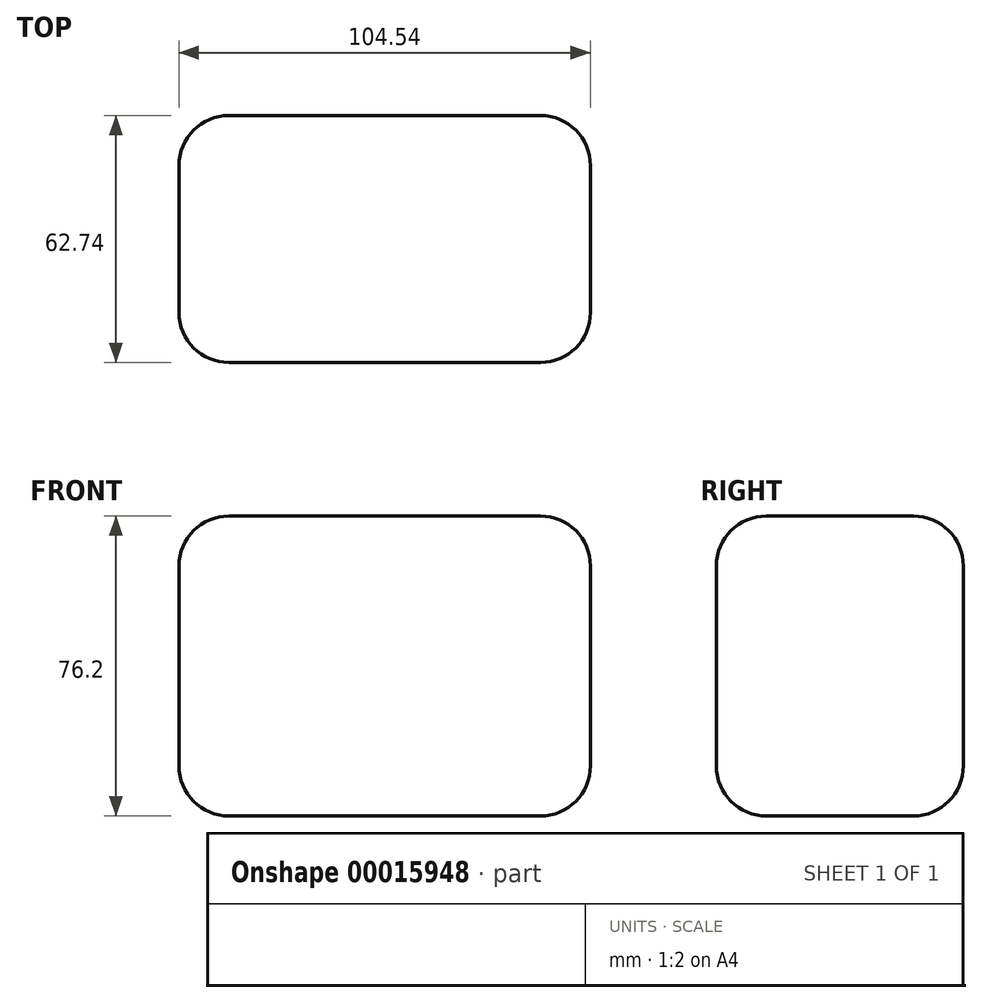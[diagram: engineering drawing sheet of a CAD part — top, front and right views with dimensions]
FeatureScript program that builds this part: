
annotation { "Feature Type Name" : "Feature", "Feature Type Description" : "" }
export const myFeature = defineFeature(function(context is Context, id is Id, definition is map)
    precondition{}
    {
        {
            var Q0;
            Q0=qCreatedBy(makeId("Top.planeOp"),FACE);
            var sketch = newSketch(context, id + "F0", { "sketchPlane" : qUnion([Q0])});
            skLineSegment(sketch, "E0.bottom", {"start": v(0, -26.62) * mm, "end": v(-104.54, -26.62) * mm});
            skLineSegment(sketch, "E0.top", {"start": v(0, 36.12) * mm, "end": v(-104.54, 36.12) * mm});
            skLineSegment(sketch, "E0.left", {"start": v(0, -26.62) * mm, "end": v(0, 36.12) * mm});
            skLineSegment(sketch, "E0.right", {"start": v(-104.54, -26.62) * mm, "end": v(-104.54, 36.12) * mm});
            skSolve(sketch);
        }
        {
            var Q0;
            Q0=makeQuery(id+"F0.imprint","IMPRINT",FACE,{"disambiguationData":[TD([[makeQuery(id+"F0.imprint","IMPRINT",EDGE,{"derivedFrom":sQuery(id+"F0.wireOp",EDGE,"E0.bottom")}),-1.0]])]});
            extrude(context, id + "F1", {"entities" : qUnion([Q0]), "depth" : 76.2 * mm});
        }
        {
            var Q0;
            Q0=makeQuery(id+"F1.opExtrude","SWEPT_FACE",FACE,{"disambiguationData":[OSD([sQuery(id+"F0.wireOp",EDGE,"E0.right")])]});
            fillet(context, id + "F2", {"entities" : qUnion([Q0]), "radius" : 12.7 * mm, "tangentPropagation" : true, "allowEdgeOverflow" : false});
        }
        {
            var Q0;
            Q0=makeQuery(id+"F1.opExtrude","SWEPT_FACE",FACE,{"disambiguationData":[OSD([sQuery(id+"F0.wireOp",EDGE,"E0.left")])]});
            var Q1;
            Q1=makeQuery(id+"F1.opExtrude","CAP_EDGE",EDGE,{"disambiguationData":[OSD([sQuery(id+"F0.wireOp",EDGE,"E0.bottom")])],"isStart":false});
            var Q2;
            Q2=makeQuery(id+"F1.opExtrude","CAP_EDGE",EDGE,{"disambiguationData":[OSD([sQuery(id+"F0.wireOp",EDGE,"E0.bottom")])],"isStart":true});
            var Q3;
            Q3=makeQuery(id+"F1.opExtrude","CAP_EDGE",EDGE,{"disambiguationData":[OSD([sQuery(id+"F0.wireOp",EDGE,"E0.top")])],"isStart":true});
            var Q4;
            Q4=makeQuery(id+"F1.opExtrude","CAP_EDGE",EDGE,{"disambiguationData":[OSD([sQuery(id+"F0.wireOp",EDGE,"E0.top")])],"isStart":false});
            fillet(context, id + "F3", {"entities" : qUnion([Q0, Q1, Q2, Q3, Q4]), "radius" : 12.7 * mm, "tangentPropagation" : true, "allowEdgeOverflow" : false});
        }
    });
